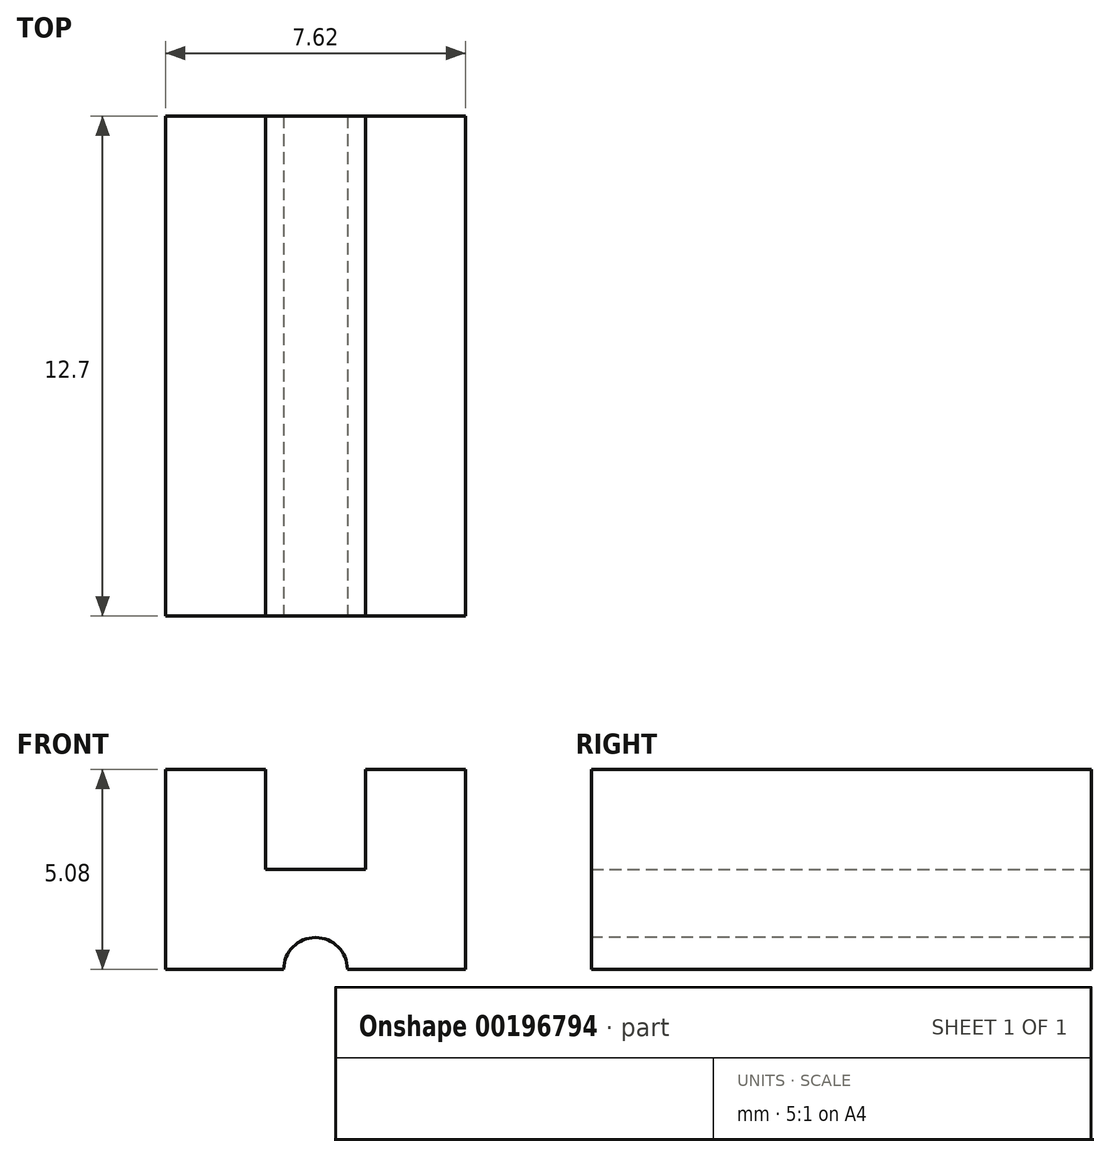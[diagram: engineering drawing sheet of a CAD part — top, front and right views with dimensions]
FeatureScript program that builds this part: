
annotation { "Feature Type Name" : "Feature", "Feature Type Description" : "" }
export const myFeature = defineFeature(function(context is Context, id is Id, definition is map)
    precondition{}
    {
        {
            var Q0;
            Q0=qCreatedBy(makeId("Front.planeOp"),FACE);
            var sketch = newSketch(context, id + "F0", { "sketchPlane" : qUnion([Q0])});
            skLineSegment(sketch, "E0", {"start": v(-3.81, 0.9) * mm, "end": v(-3.81, -4.19) * mm});
            skLineSegment(sketch, "E1.MirrorCS", {"start": v(3.81, 0.9) * mm, "end": v(3.81, -4.19) * mm});
            skLineSegment(sketch, "E2", {"start": v(-3.81, 0.9) * mm, "end": v(-1.27, 0.9) * mm});
            skLineSegment(sketch, "E3", {"start": v(-1.27, 0.9) * mm, "end": v(-1.27, -1.65) * mm});
            skLineSegment(sketch, "E4.MirrorCS", {"start": v(3.81, 0.9) * mm, "end": v(1.27, 0.9) * mm});
            skLineSegment(sketch, "E5.MirrorCS", {"start": v(1.27, 0.9) * mm, "end": v(1.27, -1.65) * mm});
            skLineSegment(sketch, "E6", {"start": v(-1.27, -1.65) * mm, "end": v(1.27, -1.65) * mm});
            skLineSegment(sketch, "E7", {"start": v(3.81, -4.19) * mm, "end": v(-3.81, -4.19) * mm});
            skSolve(sketch);
        }
        {
            var Q0;
            Q0=makeQuery(id+"F0.imprint","IMPRINT",FACE,{"disambiguationData":[TD([[makeQuery(id+"F0.imprint","IMPRINT",EDGE,{"derivedFrom":sQuery(id+"F0.wireOp",EDGE,"E0")}),1.0]])]});
            extrude(context, id + "F1", {"entities" : qUnion([Q0]), "depth" : 12.7 * mm});
        }
        {
            var Q0;
            Q0=makeQuery(id+"F1.opExtrude","CAP_FACE",FACE,{"disambiguationData":[OSD([sQuery(id+"F0.wireOp",EDGE,"E0"),sQuery(id+"F0.wireOp",EDGE,"E1.MirrorCS"),sQuery(id+"F0.wireOp",EDGE,"E2"),sQuery(id+"F0.wireOp",EDGE,"E3"),sQuery(id+"F0.wireOp",EDGE,"E4.MirrorCS"),sQuery(id+"F0.wireOp",EDGE,"E5.MirrorCS"),sQuery(id+"F0.wireOp",EDGE,"E6"),sQuery(id+"F0.wireOp",EDGE,"E7")])],"isStart":false});
            var sketch = newSketch(context, id + "F2", { "sketchPlane" : qUnion([Q0])});
            skCircle(sketch, "E8", {"center": v(0, -4.19) * mm, "radius": 0.8 * mm});
            skSolve(sketch);
        }
        {
            var Q0;
            Q0 = qSketchRegion(id + "F2", true);
            extrude(context, id + "F3", {"entities" : qUnion([Q0]), "operationType" : NewBodyOperationType.REMOVE, "oppositeDirection" : true, "depth" : 25.4 * mm});
        }
    });
